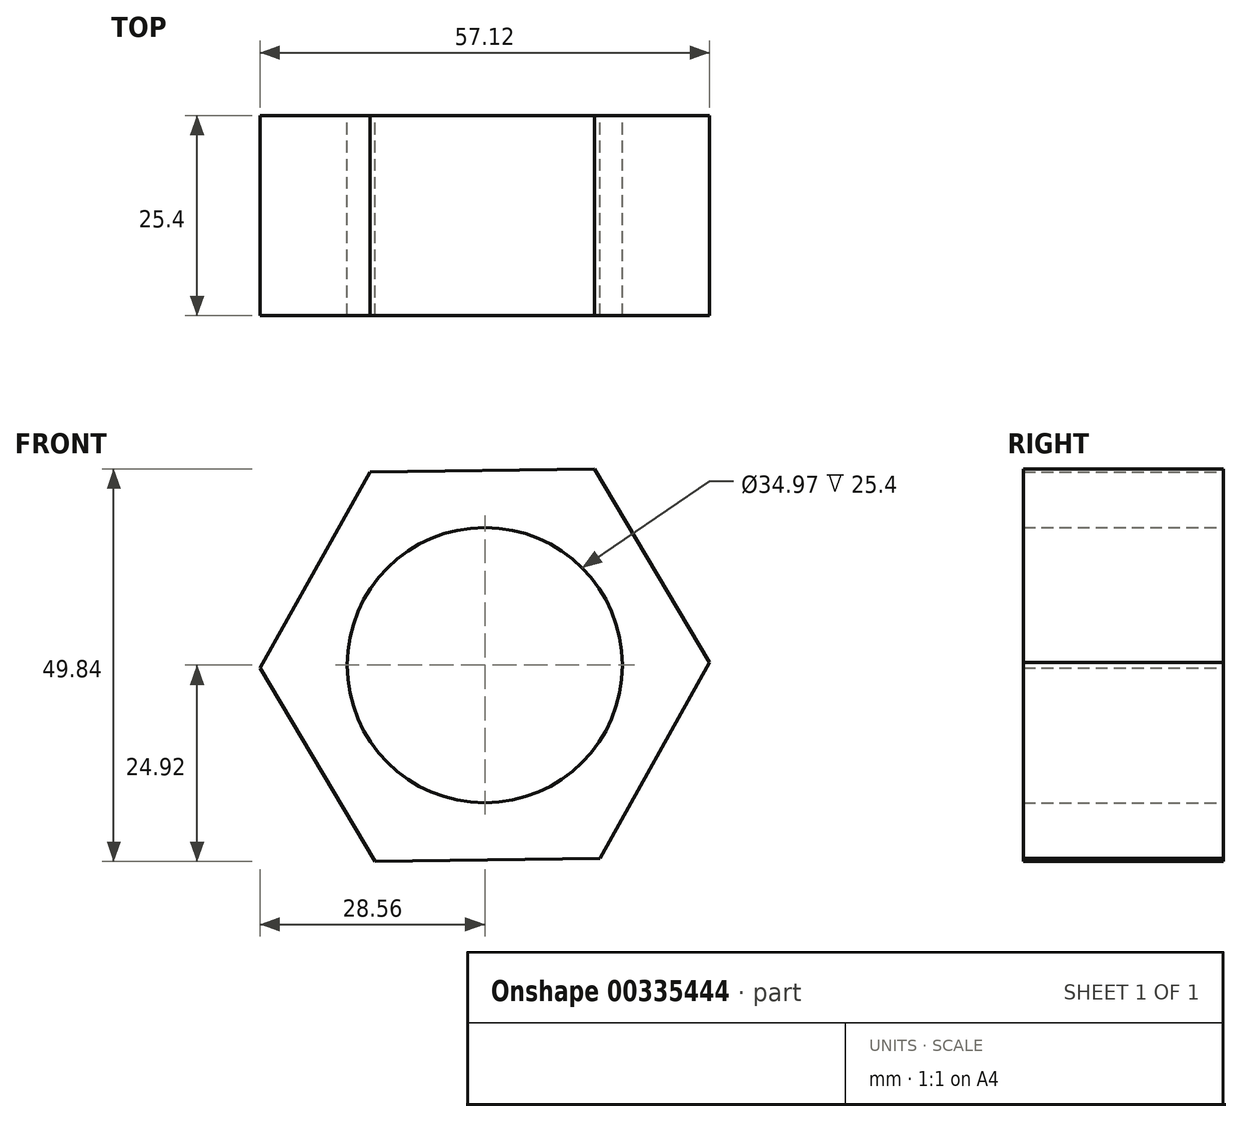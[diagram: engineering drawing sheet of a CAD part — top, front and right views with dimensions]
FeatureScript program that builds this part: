
annotation { "Feature Type Name" : "Feature", "Feature Type Description" : "" }
export const myFeature = defineFeature(function(context is Context, id is Id, definition is map)
    precondition{}
    {
        {
            var Q0;
            Q0=qCreatedBy(makeId("Front.planeOp"),FACE);
            var sketch = newSketch(context, id + "F0", { "sketchPlane" : qUnion([Q0])});
            skCircle(sketch, "E0.cCircle", {"center": v(0, 0) * mm, "radius": 24.74 * mm, "construction": true});
            skLineSegment(sketch, "E0.0", {"start": v(-28.56, -0.37) * mm, "end": v(-14.6, 24.55) * mm});
            skLineSegment(sketch, "E0.1", {"start": v(-14.6, 24.55) * mm, "end": v(13.96, 24.92) * mm});
            skLineSegment(sketch, "E0.2", {"start": v(13.96, 24.92) * mm, "end": v(28.56, 0.37) * mm});
            skLineSegment(sketch, "E0.3", {"start": v(28.56, 0.37) * mm, "end": v(14.6, -24.55) * mm});
            skLineSegment(sketch, "E0.4", {"start": v(14.6, -24.55) * mm, "end": v(-13.96, -24.92) * mm});
            skLineSegment(sketch, "E0.5", {"start": v(-13.96, -24.92) * mm, "end": v(-28.56, -0.37) * mm});
            skPoint(sketch, "E0.0.midPoint", {"position": v(-21.59, 12.09) * mm});
            skCircle(sketch, "E1", {"center": v(0, 0) * mm, "radius": 17.48 * mm});
            skSolve(sketch);
        }
        {
            var Q0;
            Q0 = qSketchRegion(id + "F0", true);
            extrude(context, id + "F1", {"entities" : qUnion([Q0]), "depth" : 25.4 * mm});
        }
        {
            var Q0;
            Q0 = qSketchRegion(id + "F0", true);
            extrude(context, id + "F2", {"entities" : qUnion([Q0]), "operationType" : NewBodyOperationType.ADD, "depth" : 25.4 * mm});
        }
    });
